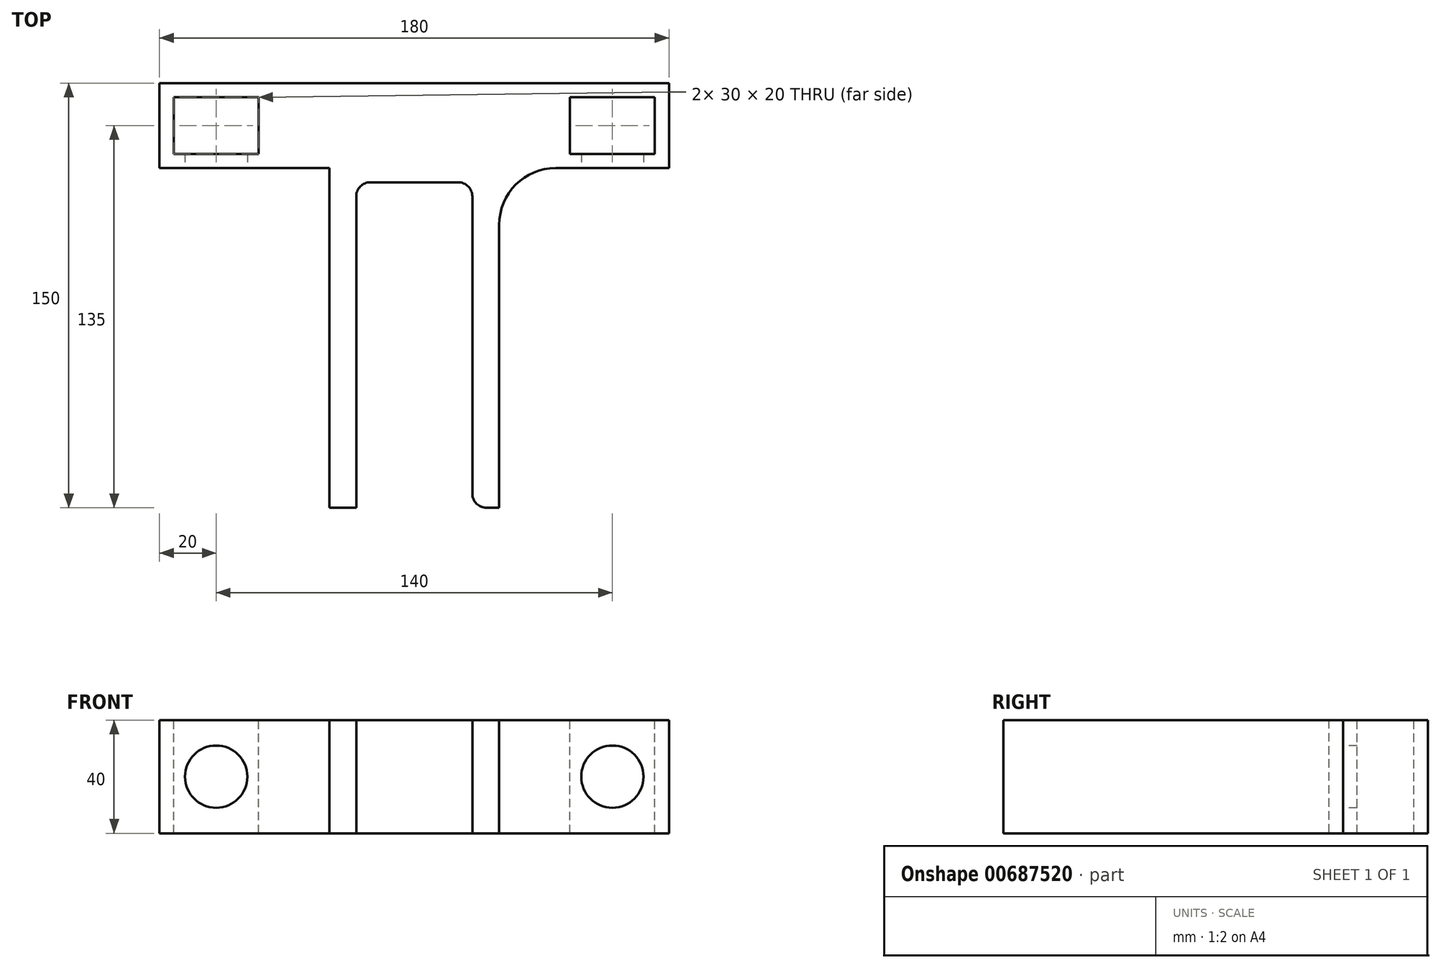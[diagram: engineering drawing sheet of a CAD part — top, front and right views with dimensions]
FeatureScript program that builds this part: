
annotation { "Feature Type Name" : "Feature", "Feature Type Description" : "" }
export const myFeature = defineFeature(function(context is Context, id is Id, definition is map)
    precondition{}
    {
        {
            var Q0;
            Q0=qCreatedBy(makeId("Front.planeOp"),FACE);
            var sketch = newSketch(context, id + "F0", { "sketchPlane" : qUnion([Q0])});
            skLineSegment(sketch, "E0.bottom", {"start": v(-90, 26.57) * mm, "end": v(90, 26.57) * mm});
            skLineSegment(sketch, "E0.top", {"start": v(-90, -13.43) * mm, "end": v(90, -13.43) * mm});
            skLineSegment(sketch, "E0.left", {"start": v(-90, 26.57) * mm, "end": v(-90, -13.43) * mm});
            skLineSegment(sketch, "E0.right", {"start": v(90, 26.57) * mm, "end": v(90, -13.43) * mm});
            skSolve(sketch);
        }
        {
            var Q0;
            Q0=qSketchRegion(id+"F0",true);
            var Q1;
            Q1=makeQuery(id+"F0.imprint","IMPRINT",FACE,{"disambiguationData":[TD([[makeQuery(id+"F0.imprint","IMPRINT",EDGE,{"derivedFrom":sQuery(id+"F0.wireOp",EDGE,"E0.bottom")}),-1.0]])]});
            extrude(context, id + "F1", {"entities" : qUnion([Q0, Q1]), "endBound" : BoundingType.SYMMETRIC, "depth" : 30 * mm, "offsetDistance" : 25 * mm});
        }
        {
            var Q0;
            Q0=makeQuery(id+"F1.opExtrude","CAP_FACE",FACE,{"disambiguationData":[OSD([sQuery(id+"F0.wireOp",EDGE,"E0.bottom"),sQuery(id+"F0.wireOp",EDGE,"E0.top"),sQuery(id+"F0.wireOp",EDGE,"E0.left"),sQuery(id+"F0.wireOp",EDGE,"E0.right")])],"isStart":false});
            var sketch = newSketch(context, id + "F2", { "sketchPlane" : qUnion([Q0])});
            skLineSegment(sketch, "E1.bottom", {"start": v(-30, 26.57) * mm, "end": v(30, 26.57) * mm});
            skLineSegment(sketch, "E1.top", {"start": v(-30, -13.43) * mm, "end": v(30, -13.43) * mm});
            skLineSegment(sketch, "E1.left", {"start": v(-30, 26.57) * mm, "end": v(-30, -13.43) * mm});
            skLineSegment(sketch, "E1.right", {"start": v(30, 26.57) * mm, "end": v(30, -13.43) * mm});
            skSolve(sketch);
        }
        {
            var Q0;
            Q0=qSketchRegion(id+"F2",true);
            var Q1;
            Q1=makeQuery(id+"F2.imprint","IMPRINT",FACE,{"disambiguationData":[TD([[makeQuery(id+"F2.imprint","IMPRINT",EDGE,{"derivedFrom":sQuery(id+"F2.wireOp",EDGE,"E1.bottom")}),-1.0]])]});
            extrude(context, id + "F3", {"entities" : qUnion([Q0, Q1]), "operationType" : NewBodyOperationType.ADD, "depth" : 120 * mm, "offsetDistance" : 25 * mm});
        }
        {
            var Q0;
            Q0=makeQuery(id+"F3.opExtrude","CAP_FACE",FACE,{"disambiguationData":[OSD([sQuery(id+"F2.wireOp",EDGE,"E1.bottom"),sQuery(id+"F2.wireOp",EDGE,"E1.top"),sQuery(id+"F2.wireOp",EDGE,"E1.left"),sQuery(id+"F2.wireOp",EDGE,"E1.right")])],"isStart":false});
            var sketch = newSketch(context, id + "F4", { "sketchPlane" : qUnion([Q0])});
            skLineSegment(sketch, "E2.bottom", {"start": v(-20.5, 26.57) * mm, "end": v(20.5, 26.57) * mm});
            skLineSegment(sketch, "E2.top", {"start": v(-20.5, -13.43) * mm, "end": v(20.5, -13.43) * mm});
            skLineSegment(sketch, "E2.left", {"start": v(-20.5, 26.57) * mm, "end": v(-20.5, -13.43) * mm});
            skLineSegment(sketch, "E2.right", {"start": v(20.5, 26.57) * mm, "end": v(20.5, -13.43) * mm});
            skSolve(sketch);
        }
        {
            var Q0;
            Q0=makeQuery(id+"F4.imprint","IMPRINT",FACE,{"disambiguationData":[TD([[makeQuery(id+"F4.imprint","IMPRINT",EDGE,{"derivedFrom":sQuery(id+"F4.wireOp",EDGE,"E2.bottom")}),-1.0]])]});
            extrude(context, id + "F5", {"entities" : qUnion([Q0]), "operationType" : NewBodyOperationType.REMOVE, "oppositeDirection" : true, "depth" : 115 * mm, "offsetDistance" : 25 * mm});
        }
        {
            var Q0;
            Q0=makeQuery(id+"F3.opExtrude","CAP_EDGE",EDGE,{"disambiguationData":[OSD([sQuery(id+"F2.wireOp",EDGE,"E1.left")])],"isStart":true});
            var Q1;
            Q1=makeQuery(id+"F3.opExtrude","CAP_EDGE",EDGE,{"disambiguationData":[OSD([sQuery(id+"F2.wireOp",EDGE,"E1.right")])],"isStart":true});
            fillet(context, id + "F6", {"entities" : qUnion([Q0, Q1]), "radius" : 20 * mm, "tangentPropagation" : true, "allowEdgeOverflow" : false});
        }
        {
            var Q0;
            Q0=makeQuery(id+"F5.boolean.opBoolean","COPY",EDGE,{"derivedFrom":makeQuery(id+"F5.opExtrude","CAP_EDGE",EDGE,{"disambiguationData":[OSD([sQuery(id+"F4.wireOp",EDGE,"E2.left")])],"isStart":false})});
            var Q1;
            Q1=makeQuery(id+"F5.boolean.opBoolean","COPY",EDGE,{"derivedFrom":makeQuery(id+"F5.opExtrude","CAP_EDGE",EDGE,{"disambiguationData":[OSD([sQuery(id+"F4.wireOp",EDGE,"E2.right")])],"isStart":false})});
            var Q2;
            Q2=makeQuery(id+"F5.boolean.opBoolean","COPY",EDGE,{"derivedFrom":makeQuery(id+"F5.opExtrude","CAP_EDGE",EDGE,{"disambiguationData":[OSD([sQuery(id+"F4.wireOp",EDGE,"E2.left")])],"isStart":true})});
            var Q3;
            Q3=makeQuery(id+"F5.boolean.opBoolean","COPY",EDGE,{"derivedFrom":makeQuery(id+"F5.opExtrude","CAP_EDGE",EDGE,{"disambiguationData":[OSD([sQuery(id+"F4.wireOp",EDGE,"E2.right")])],"isStart":true})});
            fillet(context, id + "F7", {"entities" : qUnion([Q0, Q1, Q2, Q3]), "radius" : 5 * mm, "tangentPropagation" : true, "allowEdgeOverflow" : false});
        }
        {
            var Q0;
            Q0=makeQuery(id+"F3.boolean.opBoolean","MERGE",FACE,{"derivedFrom":[makeQuery(id+"F1.opExtrude","SWEPT_FACE",FACE,{"disambiguationData":[OSD([sQuery(id+"F0.wireOp",EDGE,"E0.bottom")])]}),makeQuery(id+"F3.opExtrude","SWEPT_FACE",FACE,{"disambiguationData":[OSD([sQuery(id+"F2.wireOp",EDGE,"E1.bottom")])]})]});
            var sketch = newSketch(context, id + "F8", { "sketchPlane" : qUnion([Q0])});
            skLineSegment(sketch, "E3.bottom", {"start": v(-85, -10) * mm, "end": v(-55, -10) * mm});
            skLineSegment(sketch, "E3.top", {"start": v(-85, 10) * mm, "end": v(-55, 10) * mm});
            skLineSegment(sketch, "E3.left", {"start": v(-85, -10) * mm, "end": v(-85, 10) * mm});
            skLineSegment(sketch, "E3.right", {"start": v(-55, -10) * mm, "end": v(-55, 10) * mm});
            skSolve(sketch);
        }
        {
            var Q0;
            Q0=qSketchRegion(id+"F8",true);
            extrude(context, id + "F9", {"entities" : qUnion([Q0]), "operationType" : NewBodyOperationType.REMOVE, "oppositeDirection" : true, "depth" : 40 * mm, "offsetDistance" : 25 * mm});
        }
        {
            var Q0;
            Q0=makeQuery(id+"F3.boolean.opBoolean","MERGE",FACE,{"derivedFrom":[makeQuery(id+"F1.opExtrude","SWEPT_FACE",FACE,{"disambiguationData":[OSD([sQuery(id+"F0.wireOp",EDGE,"E0.bottom")])]}),makeQuery(id+"F3.opExtrude","SWEPT_FACE",FACE,{"disambiguationData":[OSD([sQuery(id+"F2.wireOp",EDGE,"E1.bottom")])]})]});
            var sketch = newSketch(context, id + "F10", { "sketchPlane" : qUnion([Q0])});
            skLineSegment(sketch, "E4.bottom", {"start": v(85, 10) * mm, "end": v(55, 10) * mm});
            skLineSegment(sketch, "E4.top", {"start": v(85, -10) * mm, "end": v(55, -10) * mm});
            skLineSegment(sketch, "E4.left", {"start": v(85, 10) * mm, "end": v(85, -10) * mm});
            skLineSegment(sketch, "E4.right", {"start": v(55, 10) * mm, "end": v(55, -10) * mm});
            skSolve(sketch);
        }
        {
            var Q0;
            Q0=qSketchRegion(id+"F10",true);
            extrude(context, id + "F11", {"entities" : qUnion([Q0]), "operationType" : NewBodyOperationType.REMOVE, "oppositeDirection" : true, "depth" : 40 * mm, "offsetDistance" : 25 * mm});
        }
        {
            var Q0;
            {var subQ0=sQuery(id+"F0.wireOp",EDGE,"E0.left");var subQ1=sQuery(id+"F0.wireOp",EDGE,"E0.top");var subQ2=sQuery(id+"F0.wireOp",EDGE,"E0.bottom");Q0=makeQuery(id+"F3.boolean.opBoolean","SPLIT",FACE,{"disambiguationData":[TD([makeQuery(id+"F1.opExtrude","SWEPT_FACE",FACE,{"disambiguationData":[OSD([subQ0])]})])],"derivedFrom":makeQuery(id+"F1.opExtrude","CAP_FACE",FACE,{"disambiguationData":[OSD([subQ2,subQ1,subQ0,sQuery(id+"F0.wireOp",EDGE,"E0.right")])],"isStart":false})});}
            var sketch = newSketch(context, id + "F12", { "sketchPlane" : qUnion([Q0])});
            skPoint(sketch, "E5", {"position": v(-70, 6.57) * mm});
            skPoint(sketch, "E5.positionSnap0", {"position": v(-70, -13.43) * mm});
            skPoint(sketch, "E5.positionSnap1", {"position": v(-90, 6.57) * mm});
            skSolve(sketch);
        }
        {
            var Q0;
            Q0=sQuery(id+"F12.wireOp",VERTEX,"E5");
            var Q1;
            Q1=makeQuery(id+"F1.opExtrude","SWEPT_BODY",BODY,{"disambiguationData":[OSD([sQuery(id+"F0.wireOp",EDGE,"E0.bottom"),sQuery(id+"F0.wireOp",EDGE,"E0.top"),sQuery(id+"F0.wireOp",EDGE,"E0.left"),sQuery(id+"F0.wireOp",EDGE,"E0.right")])]});
            hole(context, id + "F13", {"style" : HoleStyle.SIMPLE, "endStyle" : HoleEndStyle.BLIND, "standardTappedOrClearance" : lookupTablePath({ "fit" : "Normal", "standard" : "ISO", "size" : "M20", "type" : "Clearance" }), "standardBlindInLast" : lookupTablePath({ "fit" : "Standard", "standard" : "ISO", "size" : "M20", "type" : "Clearance" }), "holeDiameter" : 22 * mm, "majorDiameter" : 5 * mm, "holeDepth" : 12 * mm, "isTappedThrough" : true, "tappedDepth" : 12 * mm, "tapClearance" : 3, "locations" : qUnion([Q0]), "scope" : qUnion([Q1])});
        }
        {
            var Q0;
            {var subQ0=sQuery(id+"F0.wireOp",EDGE,"E0.top");var subQ1=sQuery(id+"F0.wireOp",EDGE,"E0.right");var subQ2=sQuery(id+"F0.wireOp",EDGE,"E0.bottom");Q0=makeQuery(id+"F3.boolean.opBoolean","SPLIT",FACE,{"disambiguationData":[TD([makeQuery(id+"F1.opExtrude","SWEPT_FACE",FACE,{"disambiguationData":[OSD([subQ1])]})])],"derivedFrom":makeQuery(id+"F1.opExtrude","CAP_FACE",FACE,{"disambiguationData":[OSD([subQ2,subQ0,sQuery(id+"F0.wireOp",EDGE,"E0.left"),subQ1])],"isStart":false})});}
            var sketch = newSketch(context, id + "F14", { "sketchPlane" : qUnion([Q0])});
            skPoint(sketch, "E6", {"position": v(70, 6.57) * mm});
            skPoint(sketch, "E6.positionSnap0", {"position": v(70, 26.57) * mm});
            skPoint(sketch, "E6.positionSnap1", {"position": v(90, 6.57) * mm});
            skSolve(sketch);
        }
        {
            var Q0;
            Q0=sQuery(id+"F14.wireOp",VERTEX,"E6");
            var Q1;
            Q1=makeQuery(id+"F1.opExtrude","SWEPT_BODY",BODY,{"disambiguationData":[OSD([sQuery(id+"F0.wireOp",EDGE,"E0.bottom"),sQuery(id+"F0.wireOp",EDGE,"E0.top"),sQuery(id+"F0.wireOp",EDGE,"E0.left"),sQuery(id+"F0.wireOp",EDGE,"E0.right")])]});
            hole(context, id + "F15", {"style" : HoleStyle.SIMPLE, "endStyle" : HoleEndStyle.BLIND, "standardTappedOrClearance" : lookupTablePath({ "fit" : "Normal", "standard" : "ISO", "size" : "M20", "type" : "Clearance" }), "standardBlindInLast" : lookupTablePath({ "fit" : "Standard", "standard" : "ISO", "size" : "M20", "type" : "Clearance" }), "holeDiameter" : 22 * mm, "majorDiameter" : 5 * mm, "holeDepth" : 12 * mm, "isTappedThrough" : true, "tappedDepth" : 12 * mm, "tapClearance" : 3, "locations" : qUnion([Q0]), "scope" : qUnion([Q1])});
        }
    });
